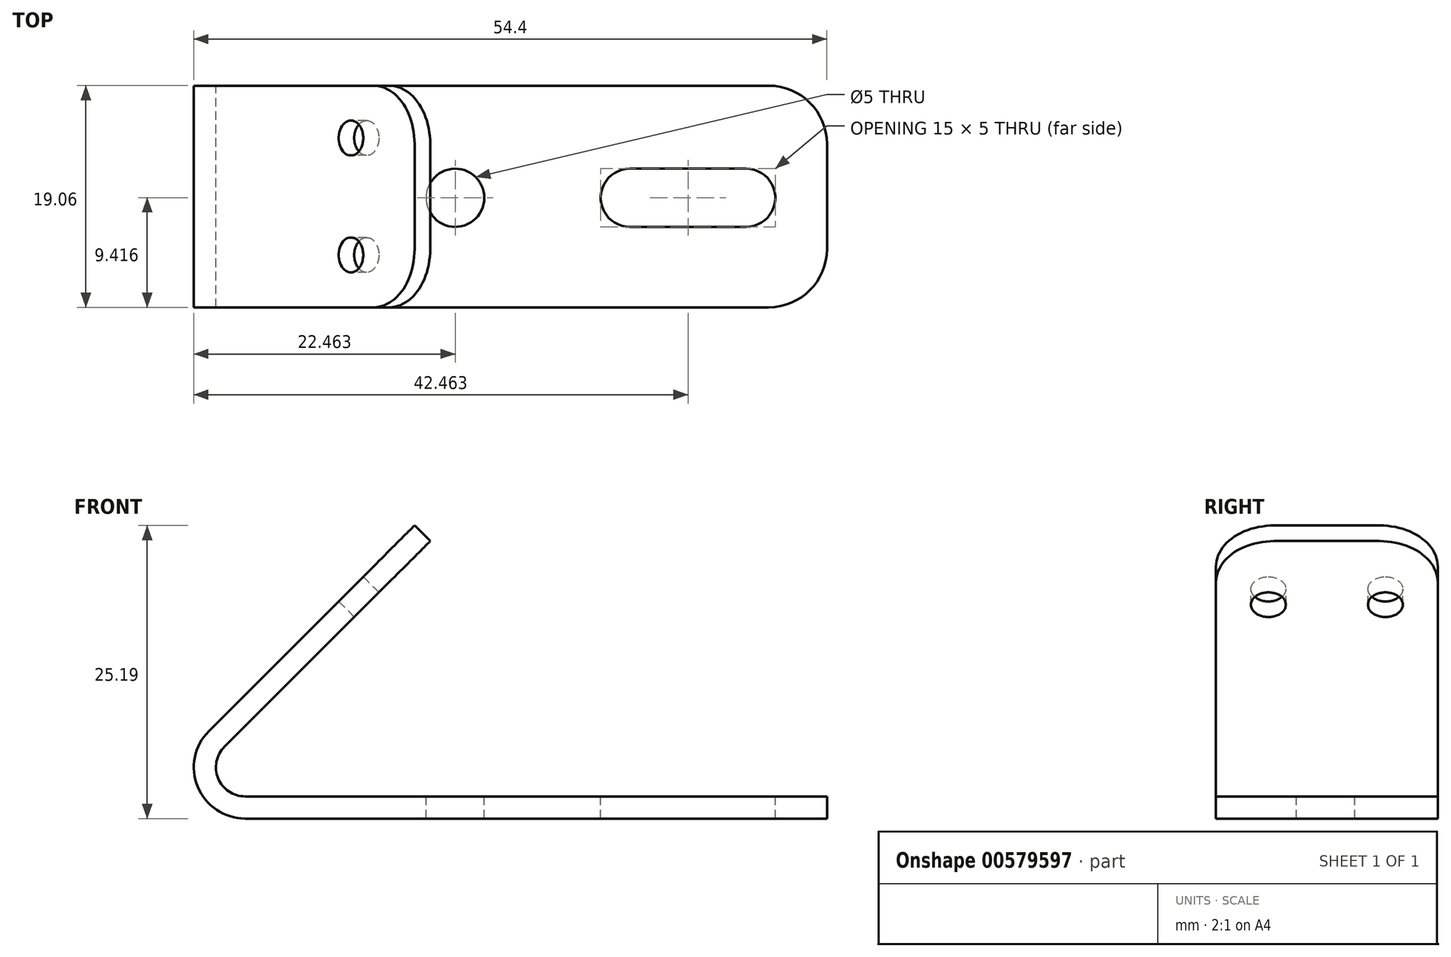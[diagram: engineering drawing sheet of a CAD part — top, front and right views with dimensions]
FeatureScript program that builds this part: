
annotation { "Feature Type Name" : "Feature", "Feature Type Description" : "" }
export const myFeature = defineFeature(function(context is Context, id is Id, definition is map)
    precondition{}
    {
        {
            var Q0;
            Q0=qCreatedBy(makeId("Front.planeOp"),FACE);
            var sketch = newSketch(context, id + "F0", { "sketchPlane" : qUnion([Q0])});
            skLineSegment(sketch, "E0", {"start": v(-36.54, -1.9) * mm, "end": v(13.46, -1.9) * mm});
            skLineSegment(sketch, "E1", {"start": v(13.46, 0) * mm, "end": v(-47.16, 0) * mm});
            skLineSegment(sketch, "E2", {"start": v(-39.65, 5.6) * mm, "end": v(-21.97, 23.28) * mm});
            skPoint(sketch, "E3.visualSharp", {"position": v(-47.16, -1.9) * mm});
            skArc(sketch, "E3.filletArc", {"start": v(-39.65, 5.6) * mm, "mid": v(-40.6, 0.8) * mm, "end": v(-36.54, -1.9) * mm});
            skLineSegment(sketch, "E4", {"start": v(-21.97, 23.28) * mm, "end": v(-20.63, 21.94) * mm});
            skLineSegment(sketch, "E5", {"start": v(-20.63, 21.94) * mm, "end": v(-38.3, 4.26) * mm});
            skArc(sketch, "E6", {"start": v(-38.3, 4.26) * mm, "mid": v(-38.85, 1.54) * mm, "end": v(-36.54, 0) * mm});
            skLineSegment(sketch, "E7", {"start": v(13.46, 0) * mm, "end": v(13.46, -1.9) * mm});
            skSolve(sketch);
        }
        {
            var Q0;
            Q0=qCreatedBy(makeId("Top.planeOp"),FACE);
            var sketch = newSketch(context, id + "F1", { "sketchPlane" : qUnion([Q0])});
            skLineSegment(sketch, "E8.0", {"start": v(13.52, -9.64) * mm, "end": v(13.52, 9.41) * mm});
            skLineSegment(sketch, "E9.0", {"start": v(13.52, 9.41) * mm, "end": v(-36.48, 9.41) * mm});
            skLineSegment(sketch, "E10.0", {"start": v(13.52, -9.64) * mm, "end": v(-36.48, -9.64) * mm});
            skLineSegment(sketch, "E11", {"start": v(13.52, -0.11) * mm, "end": v(9.02, -0.11) * mm});
            skLineSegment(sketch, "E12", {"start": v(9.02, -0.11) * mm, "end": v(-5.98, -0.11) * mm});
            skLineSegment(sketch, "E13", {"start": v(9.02, -0.11) * mm, "end": v(9.02, 2.39) * mm});
            skCircle(sketch, "E14", {"center": v(6.52, -0.11) * mm, "radius": 2.5 * mm});
            skCircle(sketch, "E15", {"center": v(-3.48, -0.11) * mm, "radius": 2.5 * mm});
            skLineSegment(sketch, "E16", {"start": v(-3.48, 2.39) * mm, "end": v(6.52, 2.39) * mm});
            skLineSegment(sketch, "E17", {"start": v(-3.48, -2.61) * mm, "end": v(6.52, -2.61) * mm});
            skCircle(sketch, "E18", {"center": v(-18.48, -0.11) * mm, "radius": 2.5 * mm});
            skSolve(sketch);
        }
        {
            var Q0;
            Q0 = qSketchRegion(id + "F0", true);
            extrude(context, id + "F2", {"entities" : qUnion([Q0]), "endBound" : BoundingType.SYMMETRIC, "depth" : 19.05 * mm, "offsetDistance" : 25.4 * mm});
        }
        {
            var Q0;
            Q0 = qSketchRegion(id + "F1", true);
            extrude(context, id + "F3", {"entities" : qUnion([Q0]), "operationType" : NewBodyOperationType.REMOVE, "endBound" : BoundingType.THROUGH_ALL, "oppositeDirection" : true, "depth" : 25.4 * mm, "offsetDistance" : 25.4 * mm});
        }
        {
            var Q0;
            Q0=makeQuery(id+"F2.opExtrude","SWEPT_FACE",FACE,{"disambiguationData":[OSD([sQuery(id+"F0.wireOp",EDGE,"E2")])]});
            var sketch = newSketch(context, id + "F4", { "sketchPlane" : qUnion([Q0])});
            skLineSegment(sketch, "E19.0", {"start": v(9.52, 0.7) * mm, "end": v(-9.52, 0.7) * mm});
            skLineSegment(sketch, "E19.1", {"start": v(9.52, -24.3) * mm, "end": v(-9.52, -24.3) * mm});
            skLineSegment(sketch, "E19.2", {"start": v(-9.53, -24.3) * mm, "end": v(-9.53, 0.7) * mm});
            skLineSegment(sketch, "E19.3", {"start": v(9.52, -24.3) * mm, "end": v(9.52, 0.7) * mm});
            skLineSegment(sketch, "E20", {"start": v(-9.53, 0.7) * mm, "end": v(-9.53, -6.8) * mm});
            skCircle(sketch, "E21", {"center": v(-5.03, -6.8) * mm, "radius": 1.5 * mm});
            skLineSegment(sketch, "E22", {"start": v(9.52, -28.7) * mm, "end": v(-9.53, -28.7) * mm});
            skCircle(sketch, "E23", {"center": v(5.02, -6.8) * mm, "radius": 1.5 * mm});
            skSolve(sketch);
        }
        {
            var Q0;
            Q0=makeQuery(id+"F4.imprint","IMPRINT",FACE,{"disambiguationData":[TD([[makeQuery(id+"F4.imprint","IMPRINT",EDGE,{"derivedFrom":sQuery(id+"F4.wireOp",EDGE,"E21")}),1.0]])]});
            var Q1;
            Q1=makeQuery(id+"F4.imprint","IMPRINT",FACE,{"disambiguationData":[TD([[makeQuery(id+"F4.imprint","IMPRINT",EDGE,{"derivedFrom":sQuery(id+"F4.wireOp",EDGE,"E23")}),1.0]])]});
            extrude(context, id + "F5", {"entities" : qUnion([Q0, Q1]), "operationType" : NewBodyOperationType.REMOVE, "endBound" : BoundingType.UP_TO_NEXT, "oppositeDirection" : true, "depth" : 25.4 * mm, "offsetDistance" : 25.4 * mm});
        }
        {
            var Q0;
            Q0=makeQuery(id+"F2.opExtrude","CAP_EDGE",EDGE,{"disambiguationData":[OSD([sQuery(id+"F0.wireOp",EDGE,"E4")])],"isStart":true});
            var Q1;
            Q1=makeQuery(id+"F2.opExtrude","CAP_EDGE",EDGE,{"disambiguationData":[OSD([sQuery(id+"F0.wireOp",EDGE,"E7")])],"isStart":true});
            var Q2;
            Q2=makeQuery(id+"F2.opExtrude","CAP_EDGE",EDGE,{"disambiguationData":[OSD([sQuery(id+"F0.wireOp",EDGE,"E7")])],"isStart":false});
            var Q3;
            Q3=makeQuery(id+"F2.opExtrude","CAP_EDGE",EDGE,{"disambiguationData":[OSD([sQuery(id+"F0.wireOp",EDGE,"E4")])],"isStart":false});
            fillet(context, id + "F6", {"entities" : qUnion([Q0, Q1, Q2, Q3]), "radius" : 5 * mm, "tangentPropagation" : true, "allowEdgeOverflow" : false});
        }
    });
